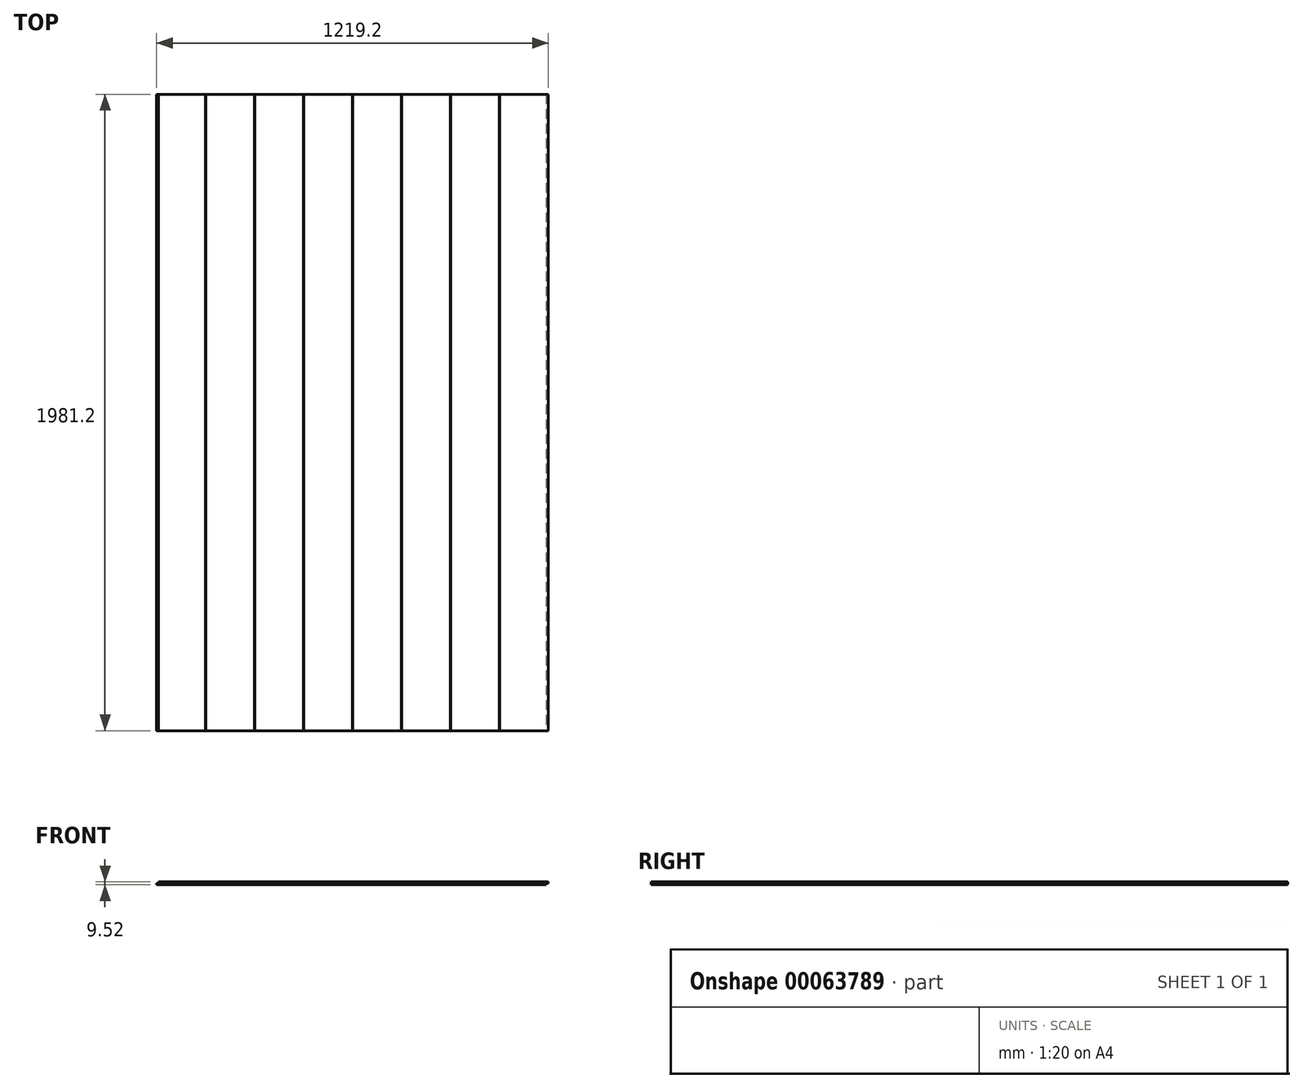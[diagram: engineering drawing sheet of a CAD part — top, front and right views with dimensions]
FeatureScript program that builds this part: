
annotation { "Feature Type Name" : "Feature", "Feature Type Description" : "" }
export const myFeature = defineFeature(function(context is Context, id is Id, definition is map)
    precondition{}
    {
        {
            var Q0;
            Q0=qCreatedBy(makeId("Top.planeOp"),FACE);
            var sketch = newSketch(context, id + "F0", { "sketchPlane" : qUnion([Q0])});
            skLineSegment(sketch, "E0.bottom", {"start": v(-609.6, 1911.45) * mm, "end": v(609.6, 1911.45) * mm});
            skLineSegment(sketch, "E0.top", {"start": v(-609.6, -523.78) * mm, "end": v(609.6, -523.78) * mm});
            skLineSegment(sketch, "E0.left", {"start": v(-609.6, 1911.45) * mm, "end": v(-609.6, -523.78) * mm});
            skLineSegment(sketch, "E0.right", {"start": v(609.6, 1911.45) * mm, "end": v(609.6, -523.78) * mm});
            skSolve(sketch);
        }
        {
            var Q0;
            Q0=qSketchRegion(id+"F0",true);
            extrude(context, id + "F1", {"entities" : qUnion([Q0]), "endBound" : BoundingType.SYMMETRIC, "depth" : 9.52 * mm});
        }
        {
            var Q0;
            Q0=makeQuery(id+"F1.opExtrude","SWEPT_FACE",FACE,{"disambiguationData":[OSD([sQuery(id+"F0.wireOp",EDGE,"E0.top")])]});
            var sketch = newSketch(context, id + "F2", { "sketchPlane" : qUnion([Q0])});
            skLineSegment(sketch, "E1", {"start": v(609.6, 0) * mm, "end": v(603.25, 0) * mm});
            skPoint(sketch, "E1.endSnap0", {"position": v(609.6, 0) * mm});
            skLineSegment(sketch, "E2", {"start": v(603.25, 0) * mm, "end": v(603.25, -4.76) * mm});
            skLineSegment(sketch, "E3", {"start": v(609.6, 0) * mm, "end": v(609.6, -4.76) * mm});
            skLineSegment(sketch, "E4", {"start": v(609.6, -4.76) * mm, "end": v(603.25, -4.76) * mm});
            skLineSegment(sketch, "E5.bottom", {"start": v(-609.6, 4.76) * mm, "end": v(-603.25, 4.76) * mm});
            skLineSegment(sketch, "E5.top", {"start": v(-609.6, 0) * mm, "end": v(-603.25, 0) * mm});
            skLineSegment(sketch, "E5.left", {"start": v(-609.6, 4.76) * mm, "end": v(-609.6, 0) * mm});
            skLineSegment(sketch, "E5.right", {"start": v(-603.25, 4.76) * mm, "end": v(-603.25, 0) * mm});
            skSolve(sketch);
        }
        {
            var Q0;
            Q0=qSketchRegion(id+"F2",true);
            extrude(context, id + "F3", {"entities" : qUnion([Q0]), "operationType" : NewBodyOperationType.REMOVE, "endBound" : BoundingType.THROUGH_ALL, "oppositeDirection" : true, "depth" : 25.4 * mm});
        }
        {
            var Q0;
            Q0=makeQuery(id+"F1.opExtrude","SWEPT_FACE",FACE,{"disambiguationData":[OSD([sQuery(id+"F0.wireOp",EDGE,"E0.top")])]});
            var sketch = newSketch(context, id + "F4", { "sketchPlane" : qUnion([Q0])});
            skLineSegment(sketch, "E6.bottom", {"start": v(-458, 4.76) * mm, "end": v(-456.4, 4.76) * mm});
            skLineSegment(sketch, "E6.top", {"start": v(-458, 3.17) * mm, "end": v(-456.4, 3.17) * mm});
            skLineSegment(sketch, "E6.left", {"start": v(-458, 4.76) * mm, "end": v(-458, 3.17) * mm});
            skLineSegment(sketch, "E6.right", {"start": v(-456.4, 4.76) * mm, "end": v(-456.4, 3.17) * mm});
            skPoint(sketch, "E7", {"position": v(-457.2, 3.17) * mm});
            skPoint(sketch, "E8.1.0.0", {"position": v(-304.8, 3.17) * mm});
            skLineSegment(sketch, "E8.1.0.1", {"start": v(-305.6, 4.76) * mm, "end": v(-304, 4.76) * mm});
            skLineSegment(sketch, "E8.1.0.2", {"start": v(-305.6, 3.17) * mm, "end": v(-304, 3.17) * mm});
            skLineSegment(sketch, "E8.1.0.3", {"start": v(-305.6, 4.76) * mm, "end": v(-305.6, 3.17) * mm});
            skLineSegment(sketch, "E8.1.0.4", {"start": v(-304, 4.76) * mm, "end": v(-304, 3.17) * mm});
            skPoint(sketch, "E8.2.0.0", {"position": v(-152.4, 3.17) * mm});
            skLineSegment(sketch, "E8.2.0.1", {"start": v(-153.2, 4.76) * mm, "end": v(-151.6, 4.76) * mm});
            skLineSegment(sketch, "E8.2.0.2", {"start": v(-153.2, 3.17) * mm, "end": v(-151.6, 3.17) * mm});
            skLineSegment(sketch, "E8.2.0.3", {"start": v(-153.2, 4.76) * mm, "end": v(-153.2, 3.17) * mm});
            skLineSegment(sketch, "E8.2.0.4", {"start": v(-151.6, 4.76) * mm, "end": v(-151.6, 3.17) * mm});
            skPoint(sketch, "E8.3.0.0", {"position": v(0, 3.17) * mm});
            skLineSegment(sketch, "E8.3.0.1", {"start": v(-0.8, 4.76) * mm, "end": v(0.8, 4.76) * mm});
            skLineSegment(sketch, "E8.3.0.2", {"start": v(-0.8, 3.17) * mm, "end": v(0.8, 3.17) * mm});
            skLineSegment(sketch, "E8.3.0.3", {"start": v(-0.8, 4.76) * mm, "end": v(-0.8, 3.17) * mm});
            skLineSegment(sketch, "E8.3.0.4", {"start": v(0.8, 4.76) * mm, "end": v(0.8, 3.17) * mm});
            skPoint(sketch, "E8.4.0.0", {"position": v(152.4, 3.17) * mm});
            skLineSegment(sketch, "E8.4.0.1", {"start": v(151.6, 4.76) * mm, "end": v(153.2, 4.76) * mm});
            skLineSegment(sketch, "E8.4.0.2", {"start": v(151.6, 3.17) * mm, "end": v(153.2, 3.17) * mm});
            skLineSegment(sketch, "E8.4.0.3", {"start": v(151.6, 4.76) * mm, "end": v(151.6, 3.17) * mm});
            skLineSegment(sketch, "E8.4.0.4", {"start": v(153.2, 4.76) * mm, "end": v(153.2, 3.17) * mm});
            skPoint(sketch, "E8.5.0.0", {"position": v(304.8, 3.17) * mm});
            skLineSegment(sketch, "E8.5.0.1", {"start": v(304, 4.76) * mm, "end": v(305.6, 4.76) * mm});
            skLineSegment(sketch, "E8.5.0.2", {"start": v(304, 3.17) * mm, "end": v(305.6, 3.17) * mm});
            skLineSegment(sketch, "E8.5.0.3", {"start": v(304, 4.76) * mm, "end": v(304, 3.17) * mm});
            skLineSegment(sketch, "E8.5.0.4", {"start": v(305.6, 4.76) * mm, "end": v(305.6, 3.17) * mm});
            skPoint(sketch, "E8.6.0.0", {"position": v(457.2, 3.17) * mm});
            skLineSegment(sketch, "E8.6.0.1", {"start": v(456.4, 4.76) * mm, "end": v(458, 4.76) * mm});
            skLineSegment(sketch, "E8.6.0.2", {"start": v(456.4, 3.17) * mm, "end": v(458, 3.17) * mm});
            skLineSegment(sketch, "E8.6.0.3", {"start": v(456.4, 4.76) * mm, "end": v(456.4, 3.17) * mm});
            skLineSegment(sketch, "E8.6.0.4", {"start": v(458, 4.76) * mm, "end": v(458, 3.17) * mm});
            skLineSegment(sketch, "E8.direction1", {"start": v(-457.2, 3.17) * mm, "end": v(-304.8, 3.17) * mm, "construction": true});
            skSolve(sketch);
        }
        {
            var Q0;
            Q0=qSketchRegion(id+"F4",true);
            extrude(context, id + "F5", {"entities" : qUnion([Q0]), "operationType" : NewBodyOperationType.REMOVE, "endBound" : BoundingType.THROUGH_ALL, "oppositeDirection" : true, "depth" : 25.4 * mm});
        }
        {
            var Q0;
            Q0=makeQuery(id+"F1.opExtrude","SWEPT_FACE",FACE,{"disambiguationData":[OSD([sQuery(id+"F0.wireOp",EDGE,"E0.left")])]});
            var sketch = newSketch(context, id + "F6", { "sketchPlane" : qUnion([Q0])});
            skPoint(sketch, "E9.0", {"position": v(-1911.45, -4.76) * mm});
            skPoint(sketch, "E10.0", {"position": v(-1911.45, 4.76) * mm});
            skLineSegment(sketch, "E11.bottom", {"start": v(-1911.45, -4.76) * mm, "end": v(-1457.42, -4.76) * mm});
            skLineSegment(sketch, "E11.top", {"start": v(-1911.45, 4.76) * mm, "end": v(-1457.42, 4.76) * mm});
            skLineSegment(sketch, "E11.left", {"start": v(-1911.45, -4.76) * mm, "end": v(-1911.45, 4.76) * mm});
            skLineSegment(sketch, "E11.right", {"start": v(-1457.42, -4.76) * mm, "end": v(-1457.42, 4.76) * mm});
            skSolve(sketch);
        }
        {
            var Q0;
            Q0 = qSketchRegion(id + "F6", true);
            extrude(context, id + "F7", {"entities" : qUnion([Q0]), "operationType" : NewBodyOperationType.REMOVE, "endBound" : BoundingType.THROUGH_ALL, "oppositeDirection" : true, "depth" : 25.4 * mm});
        }
    });
